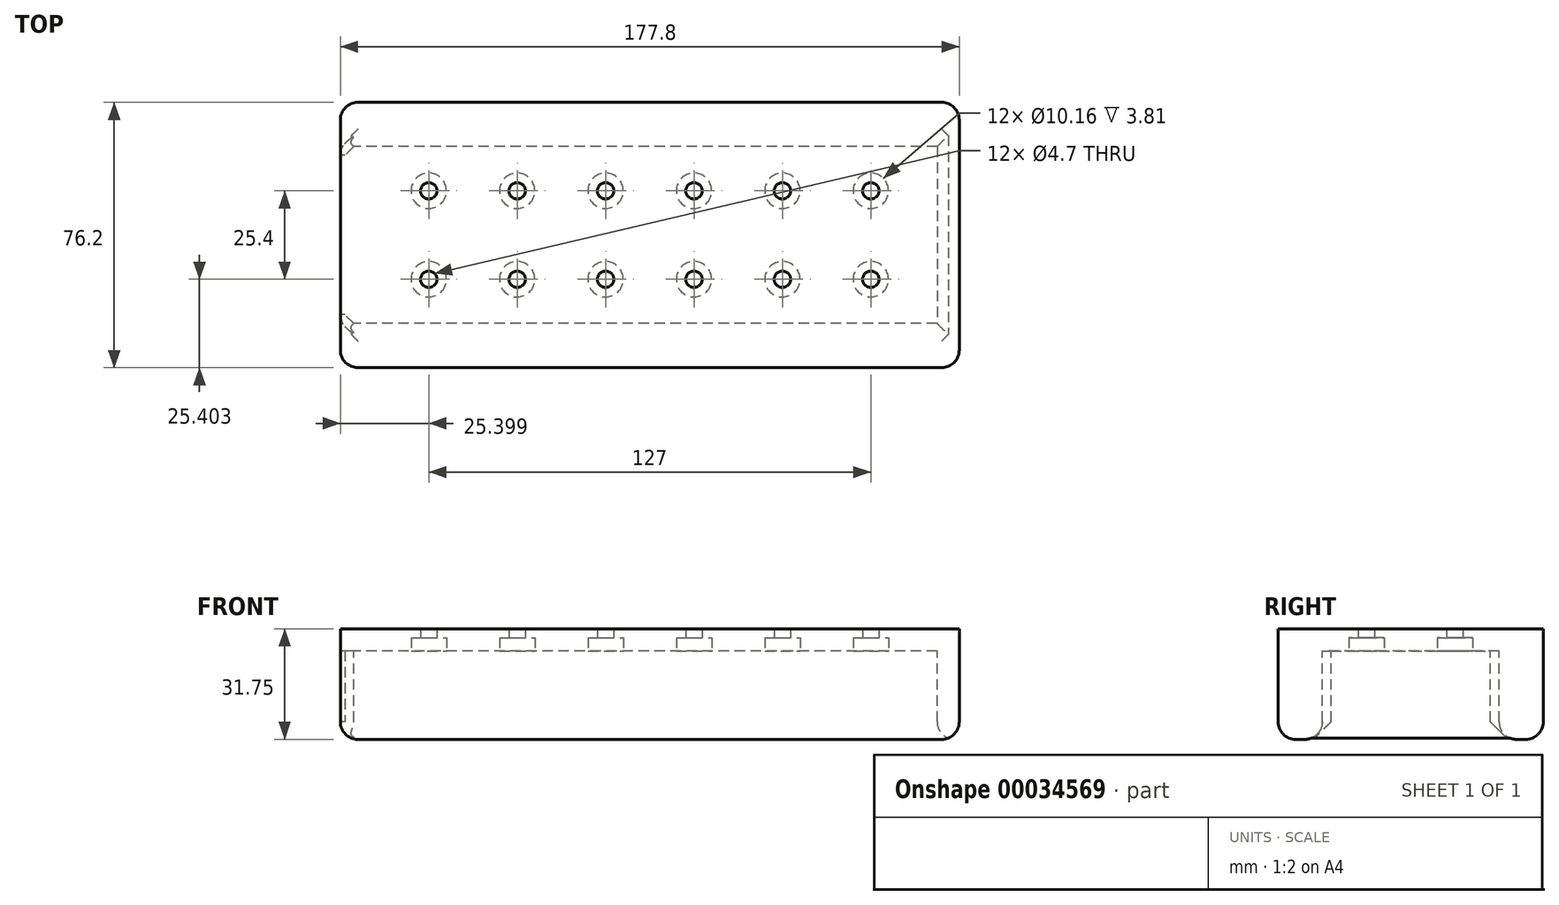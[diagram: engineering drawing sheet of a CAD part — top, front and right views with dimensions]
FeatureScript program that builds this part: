
annotation { "Feature Type Name" : "Feature", "Feature Type Description" : "" }
export const myFeature = defineFeature(function(context is Context, id is Id, definition is map)
    precondition{}
    {
        {
            var Q0;
            Q0=qCreatedBy(makeId("Top.planeOp"),FACE);
            var sketch = newSketch(context, id + "F0", { "sketchPlane" : qUnion([Q0])});
            skLineSegment(sketch, "E0.bottom", {"start": v(90.18, -46.85) * mm, "end": v(-87.62, -46.85) * mm});
            skLineSegment(sketch, "E0.top", {"start": v(90.18, 29.35) * mm, "end": v(-87.62, 29.35) * mm});
            skLineSegment(sketch, "E0.left", {"start": v(90.18, -46.85) * mm, "end": v(90.18, 29.35) * mm});
            skLineSegment(sketch, "E0.right", {"start": v(-87.62, -46.85) * mm, "end": v(-87.62, 29.35) * mm});
            skSolve(sketch);
        }
        {
            var Q0;
            Q0=makeQuery(id+"F0.imprint","IMPRINT",FACE,{"disambiguationData":[TD([[makeQuery(id+"F0.imprint","IMPRINT",EDGE,{"derivedFrom":sQuery(id+"F0.wireOp",EDGE,"E0.bottom")}),-1.0]])]});
            extrude(context, id + "F1", {"entities" : qUnion([Q0]), "depth" : 6.35 * mm});
        }
        {
            var Q0;
            Q0=makeQuery(id+"F1.opExtrude","CAP_FACE",FACE,{"disambiguationData":[OSD([sQuery(id+"F0.wireOp",EDGE,"E0.bottom"),sQuery(id+"F0.wireOp",EDGE,"E0.top"),sQuery(id+"F0.wireOp",EDGE,"E0.left"),sQuery(id+"F0.wireOp",EDGE,"E0.right")])],"isStart":true});
            var sketch = newSketch(context, id + "F2", { "sketchPlane" : qUnion([Q0])});
            skLineSegment(sketch, "E1.bottom", {"start": v(83.83, -16.65) * mm, "end": v(-81.27, -16.65) * mm});
            skLineSegment(sketch, "E1.top", {"start": v(83.83, 34.15) * mm, "end": v(-81.27, 34.15) * mm});
            skLineSegment(sketch, "E1.left", {"start": v(83.83, -16.65) * mm, "end": v(83.83, 34.15) * mm});
            skLineSegment(sketch, "E1.right", {"start": v(-81.27, -16.65) * mm, "end": v(-81.27, 34.15) * mm});
            skLineSegment(sketch, "E2.bottom", {"start": v(-81.27, -14.11) * mm, "end": v(-87.62, -14.11) * mm});
            skLineSegment(sketch, "E2.top", {"start": v(-81.27, 31.6) * mm, "end": v(-87.62, 31.6) * mm});
            skLineSegment(sketch, "E2.left", {"start": v(-81.27, -14.11) * mm, "end": v(-81.27, 31.6) * mm});
            skLineSegment(sketch, "E2.right", {"start": v(-87.62, -14.11) * mm, "end": v(-87.62, 31.6) * mm});
            skSolve(sketch);
        }
        {
            var Q0;
            {var subQ9=sQuery(id+"F2.wireOp",EDGE,"E1.bottom");Q0=makeQuery(id+"F2.imprint","IMPRINT",FACE,{"disambiguationData":[TD([[makeQuery(id+"F2.imprint","IMPRINT",EDGE,{"derivedFrom":subQ9}),1.0]])]});}
            extrude(context, id + "F3", {"entities" : qUnion([Q0]), "operationType" : NewBodyOperationType.ADD, "depth" : 25.4 * mm});
        }
        {
            var Q0;
            Q0=makeQuery(id+"F1.opExtrude","CAP_FACE",FACE,{"disambiguationData":[OSD([sQuery(id+"F0.wireOp",EDGE,"E0.bottom"),sQuery(id+"F0.wireOp",EDGE,"E0.top"),sQuery(id+"F0.wireOp",EDGE,"E0.left"),sQuery(id+"F0.wireOp",EDGE,"E0.right")])],"isStart":true});
            var sketch = newSketch(context, id + "F4", { "sketchPlane" : qUnion([Q0])});
            skLineSegment(sketch, "E3", {"start": v(-87.62, 8.75) * mm, "end": v(83.83, 8.75) * mm});
            skCircle(sketch, "E4", {"center": v(-62.22, 21.45) * mm, "radius": 5.08 * mm});
            skCircle(sketch, "E5.0.1.0", {"center": v(-62.22, -3.95) * mm, "radius": 5.08 * mm});
            skCircle(sketch, "E5.1.0.0", {"center": v(-36.82, 21.45) * mm, "radius": 5.08 * mm});
            skCircle(sketch, "E5.1.1.0", {"center": v(-36.82, -3.95) * mm, "radius": 5.08 * mm});
            skCircle(sketch, "E5.2.0.0", {"center": v(-11.42, 21.45) * mm, "radius": 5.08 * mm});
            skCircle(sketch, "E5.2.1.0", {"center": v(-11.42, -3.95) * mm, "radius": 5.08 * mm});
            skCircle(sketch, "E5.3.0.0", {"center": v(13.98, 21.45) * mm, "radius": 5.08 * mm});
            skCircle(sketch, "E5.3.1.0", {"center": v(13.98, -3.95) * mm, "radius": 5.08 * mm});
            skCircle(sketch, "E5.4.0.0", {"center": v(39.38, 21.45) * mm, "radius": 5.08 * mm});
            skCircle(sketch, "E5.4.1.0", {"center": v(39.38, -3.95) * mm, "radius": 5.08 * mm});
            skCircle(sketch, "E5.5.0.0", {"center": v(64.78, 21.45) * mm, "radius": 5.08 * mm});
            skCircle(sketch, "E5.5.1.0", {"center": v(64.78, -3.95) * mm, "radius": 5.08 * mm});
            skLineSegment(sketch, "E5.direction1", {"start": v(-62.22, 21.45) * mm, "end": v(-36.82, 21.45) * mm, "construction": true});
            skLineSegment(sketch, "E5.direction2", {"start": v(-62.22, 21.45) * mm, "end": v(-62.22, -3.95) * mm, "construction": true});
            skSolve(sketch);
        }
        {
            var Q0;
            Q0 = qSketchRegion(id + "F4", true);
            extrude(context, id + "F5", {"entities" : qUnion([Q0]), "operationType" : NewBodyOperationType.REMOVE, "oppositeDirection" : true, "depth" : 3.8 * mm});
        }
        {
            var Q0;
            Q0=makeQuery(id+"F5.boolean.opBoolean","COPY",FACE,{"derivedFrom":makeQuery(id+"F5.opExtrude","CAP_FACE",FACE,{"disambiguationData":[OSD([sQuery(id+"F4.wireOp",EDGE,"E4")])],"isStart":false})});
            var sketch = newSketch(context, id + "F6", { "sketchPlane" : qUnion([Q0])});
            skCircle(sketch, "E6", {"center": v(-62.22, 21.45) * mm, "radius": 2.35 * mm});
            skCircle(sketch, "E7.0.1.0", {"center": v(-62.22, -3.95) * mm, "radius": 2.35 * mm});
            skCircle(sketch, "E7.1.0.0", {"center": v(-36.82, 21.45) * mm, "radius": 2.35 * mm});
            skCircle(sketch, "E7.1.1.0", {"center": v(-36.82, -3.95) * mm, "radius": 2.35 * mm});
            skCircle(sketch, "E7.2.0.0", {"center": v(-11.42, 21.45) * mm, "radius": 2.35 * mm});
            skCircle(sketch, "E7.2.1.0", {"center": v(-11.42, -3.95) * mm, "radius": 2.35 * mm});
            skCircle(sketch, "E7.3.0.0", {"center": v(13.98, 21.45) * mm, "radius": 2.35 * mm});
            skCircle(sketch, "E7.3.1.0", {"center": v(13.98, -3.95) * mm, "radius": 2.35 * mm});
            skCircle(sketch, "E7.4.0.0", {"center": v(39.38, 21.45) * mm, "radius": 2.35 * mm});
            skCircle(sketch, "E7.4.1.0", {"center": v(39.38, -3.95) * mm, "radius": 2.35 * mm});
            skCircle(sketch, "E7.5.0.0", {"center": v(64.78, 21.45) * mm, "radius": 2.35 * mm});
            skCircle(sketch, "E7.5.1.0", {"center": v(64.78, -3.95) * mm, "radius": 2.35 * mm});
            skLineSegment(sketch, "E7.direction1", {"start": v(-62.22, 21.45) * mm, "end": v(-36.82, 21.45) * mm, "construction": true});
            skLineSegment(sketch, "E7.direction2", {"start": v(-62.22, 21.45) * mm, "end": v(-62.22, -3.95) * mm, "construction": true});
            skSolve(sketch);
        }
        {
            var Q0;
            Q0 = qSketchRegion(id + "F6", true);
            extrude(context, id + "F7", {"entities" : qUnion([Q0]), "operationType" : NewBodyOperationType.REMOVE, "oppositeDirection" : true, "depth" : 25.4 * mm});
        }
        {
            var Q0;
            Q0=makeQuery(id+"F3.opExtrude","CAP_EDGE",EDGE,{"disambiguationData":[OSD([sQuery(id+"F2.wireOp",EDGE,"E1.top")])],"isStart":true});
            var Q1;
            Q1=makeQuery(id+"F3.opExtrude","CAP_EDGE",EDGE,{"disambiguationData":[OSD([sQuery(id+"F2.wireOp",EDGE,"E1.left")])],"isStart":true});
            var Q2;
            Q2=makeQuery(id+"F3.opExtrude","CAP_EDGE",EDGE,{"disambiguationData":[OSD([sQuery(id+"F2.wireOp",EDGE,"E1.bottom")])],"isStart":true});
            var Q3;
            Q3=makeQuery(id+"F3.opExtrude","CAP_EDGE",EDGE,{"disambiguationData":[OSD([sQuery(id+"F2.wireOp",EDGE,"E1.left")])],"isStart":false});
            var Q4;
            Q4=makeQuery(id+"F3.opExtrude","CAP_EDGE",EDGE,{"disambiguationData":[OSD([sQuery(id+"F2.wireOp",EDGE,"E1.top")])],"isStart":false});
            var Q5;
            Q5=makeQuery(id+"F3.opExtrude","CAP_EDGE",EDGE,{"disambiguationData":[OSD([sQuery(id+"F2.wireOp",EDGE,"E1.bottom")])],"isStart":false});
            var Q6;
            {var subQ0=sQuery(id+"F2.wireOp",EDGE,"E1.right");Q6=makeQuery(id+"F3.opExtrude","CAP_EDGE",EDGE,{"disambiguationData":[OSD([subQ0]),TDD([makeQuery(id+"F2.imprint","IMPRINT",EDGE,{"disambiguationData":[TD([[makeQuery(id+"F2.imprint","INTERSECT",VERTEX,{"derivedFrom":[sQuery(id+"F2.wireOp",EDGE,"E1.top"),subQ0]}),1.0]])],"derivedFrom":subQ0})])],"isStart":false});}
            var Q7;
            {var subQ0=sQuery(id+"F2.wireOp",EDGE,"E1.right");Q7=makeQuery(id+"F3.opExtrude","CAP_EDGE",EDGE,{"disambiguationData":[OSD([subQ0]),TDD([makeQuery(id+"F2.imprint","IMPRINT",EDGE,{"disambiguationData":[TD([[makeQuery(id+"F2.imprint","INTERSECT",VERTEX,{"derivedFrom":[sQuery(id+"F2.wireOp",EDGE,"E1.bottom"),subQ0]}),-1.0]])],"derivedFrom":subQ0})])],"isStart":false});}
            fillet(context, id + "F8", {"entities" : qUnion([Q0, Q1, Q2, Q3, Q4, Q5, Q6, Q7]), "radius" : 5.08 * mm, "tangentPropagation" : true, "allowEdgeOverflow" : false});
        }
        {
            var Q0;
            Q0=makeQuery(id+"F3.opExtrude","SWEPT_EDGE",EDGE,{"disambiguationData":[OSD([sQuery(id+"F2.wireOp",EDGE,"E1.right"),sQuery(id+"F2.wireOp",EDGE,"E2.top"),sQuery(id+"F2.wireOp",EDGE,"E2.left")])]});
            var Q1;
            Q1=makeQuery(id+"F3.opExtrude","SWEPT_EDGE",EDGE,{"disambiguationData":[OSD([sQuery(id+"F2.wireOp",EDGE,"E1.right"),sQuery(id+"F2.wireOp",EDGE,"E2.bottom"),sQuery(id+"F2.wireOp",EDGE,"E2.left")])]});
            chamfer(context, id + "F9", {"entities" : qUnion([Q0, Q1]), "width" : 5.08 * mm, "tangentPropagation" : true});
        }
        {
            var Q0;
            {var subQ0=sQuery(id+"F0.wireOp",EDGE,"E0.bottom");var subQ1=sQuery(id+"F0.wireOp",EDGE,"E0.right");Q0=makeQuery(id+"F3.boolean.opBoolean","MERGE",EDGE,{"derivedFrom":[makeQuery(id+"F1.opExtrude","SWEPT_EDGE",EDGE,{"disambiguationData":[OSD([subQ0,subQ1])]}),makeQuery(id+"F3.opExtrude","SWEPT_EDGE",EDGE,{"disambiguationData":[OSD([subQ0,subQ1])]})]});}
            var Q1;
            {var subQ0=sQuery(id+"F0.wireOp",EDGE,"E0.top");var subQ1=sQuery(id+"F0.wireOp",EDGE,"E0.right");Q1=makeQuery(id+"F3.boolean.opBoolean","MERGE",EDGE,{"derivedFrom":[makeQuery(id+"F1.opExtrude","SWEPT_EDGE",EDGE,{"disambiguationData":[OSD([subQ0,subQ1])]}),makeQuery(id+"F3.opExtrude","SWEPT_EDGE",EDGE,{"disambiguationData":[OSD([subQ0,subQ1])]})]});}
            var Q2;
            {var subQ0=sQuery(id+"F0.wireOp",EDGE,"E0.top");var subQ1=sQuery(id+"F0.wireOp",EDGE,"E0.left");Q2=makeQuery(id+"F3.boolean.opBoolean","MERGE",EDGE,{"derivedFrom":[makeQuery(id+"F1.opExtrude","SWEPT_EDGE",EDGE,{"disambiguationData":[OSD([subQ0,subQ1])]}),makeQuery(id+"F3.opExtrude","SWEPT_EDGE",EDGE,{"disambiguationData":[OSD([subQ0,subQ1])]})]});}
            var Q3;
            {var subQ0=sQuery(id+"F0.wireOp",EDGE,"E0.bottom");var subQ1=sQuery(id+"F0.wireOp",EDGE,"E0.left");Q3=makeQuery(id+"F3.boolean.opBoolean","MERGE",EDGE,{"derivedFrom":[makeQuery(id+"F1.opExtrude","SWEPT_EDGE",EDGE,{"disambiguationData":[OSD([subQ0,subQ1])]}),makeQuery(id+"F3.opExtrude","SWEPT_EDGE",EDGE,{"disambiguationData":[OSD([subQ0,subQ1])]})]});}
            var Q4;
            Q4=makeQuery(id+"F3.opExtrude","CAP_EDGE",EDGE,{"disambiguationData":[OSD([sQuery(id+"F0.wireOp",EDGE,"E0.top")])],"isStart":false});
            var Q5;
            Q5=makeQuery(id+"F3.opExtrude","CAP_EDGE",EDGE,{"disambiguationData":[OSD([sQuery(id+"F0.wireOp",EDGE,"E0.left")])],"isStart":false});
            var Q6;
            Q6=makeQuery(id+"F3.opExtrude","CAP_EDGE",EDGE,{"disambiguationData":[OSD([sQuery(id+"F0.wireOp",EDGE,"E0.bottom")])],"isStart":false});
            var Q7;
            {var subQ0=sQuery(id+"F0.wireOp",EDGE,"E0.right");var subQ1=makeQuery(id+"F1.opExtrude","CAP_EDGE",EDGE,{"disambiguationData":[OSD([subQ0])],"isStart":true});Q7=makeQuery(id+"F3.opExtrude","CAP_EDGE",EDGE,{"disambiguationData":[OSD([subQ0]),TDD([makeQuery(id+"F2.imprint","IMPRINT",EDGE,{"disambiguationData":[TD([[makeQuery(id+"F2.imprint","INTERSECT",VERTEX,{"derivedFrom":[makeQuery(id+"F1.opExtrude","CAP_EDGE",EDGE,{"disambiguationData":[OSD([sQuery(id+"F0.wireOp",EDGE,"E0.bottom")])],"isStart":true}),subQ1]}),-1.0]])],"derivedFrom":subQ1})])],"isStart":false});}
            var Q8;
            {var subQ0=sQuery(id+"F0.wireOp",EDGE,"E0.right");var subQ1=makeQuery(id+"F1.opExtrude","CAP_EDGE",EDGE,{"disambiguationData":[OSD([subQ0])],"isStart":true});Q8=makeQuery(id+"F3.opExtrude","CAP_EDGE",EDGE,{"disambiguationData":[OSD([subQ0]),TDD([makeQuery(id+"F2.imprint","IMPRINT",EDGE,{"disambiguationData":[TD([[makeQuery(id+"F2.imprint","INTERSECT",VERTEX,{"derivedFrom":[makeQuery(id+"F1.opExtrude","CAP_EDGE",EDGE,{"disambiguationData":[OSD([sQuery(id+"F0.wireOp",EDGE,"E0.top")])],"isStart":true}),subQ1]}),1.0]])],"derivedFrom":subQ1})])],"isStart":false});}
            fillet(context, id + "F10", {"entities" : qUnion([Q0, Q1, Q2, Q3, Q4, Q5, Q6, Q7, Q8]), "radius" : 5.08 * mm, "tangentPropagation" : true, "allowEdgeOverflow" : false});
        }
    });
